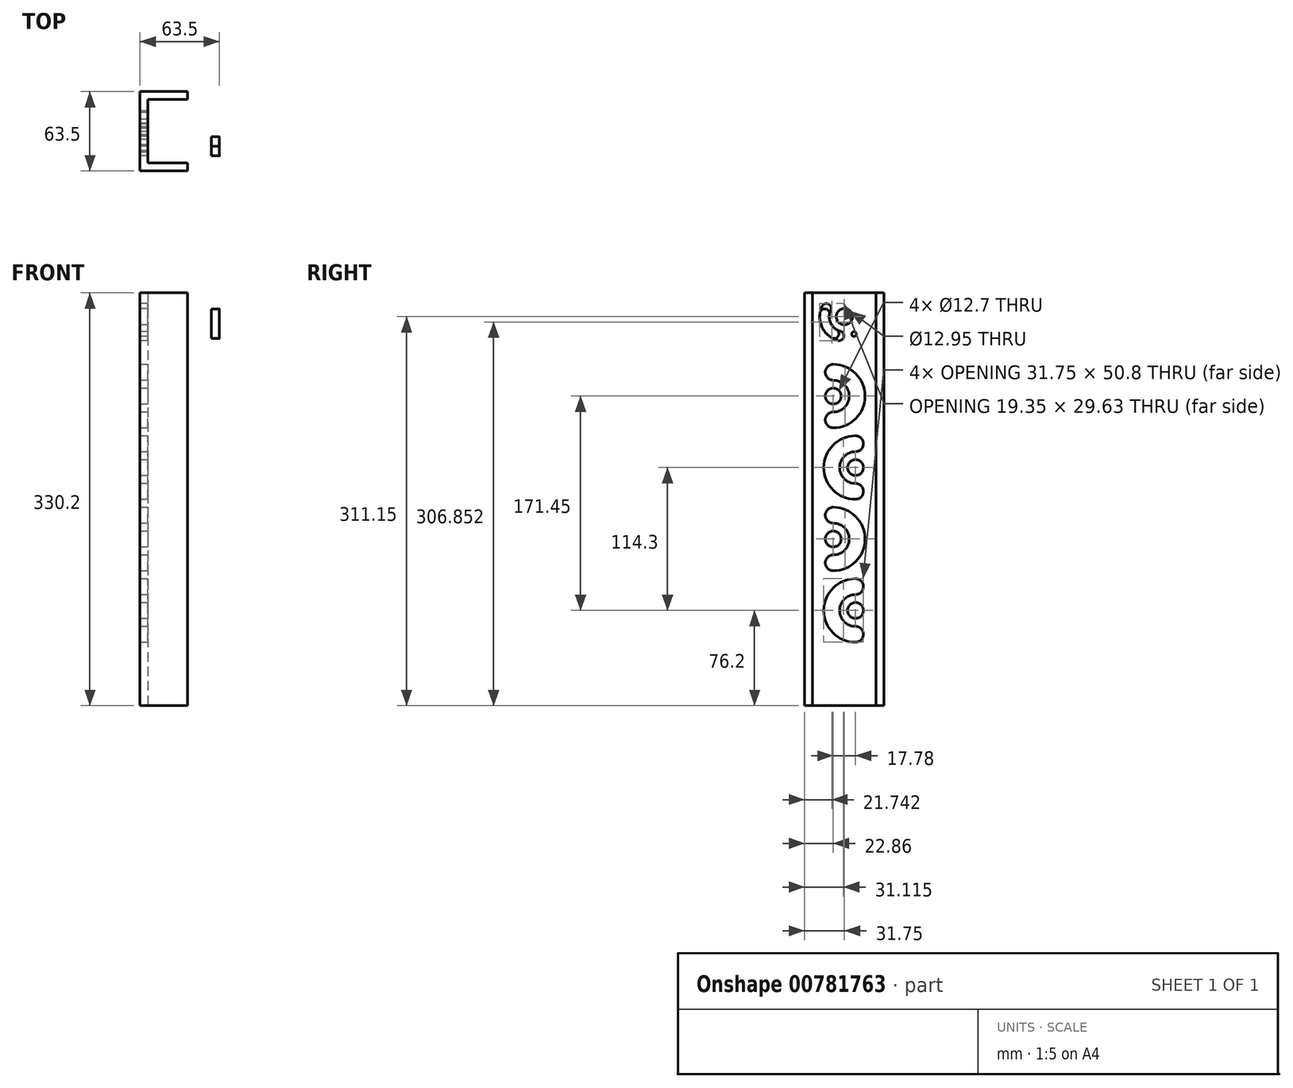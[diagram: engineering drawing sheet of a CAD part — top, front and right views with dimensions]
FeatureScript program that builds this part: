
annotation { "Feature Type Name" : "Feature", "Feature Type Description" : "" }
export const myFeature = defineFeature(function(context is Context, id is Id, definition is map)
    precondition{}
    {
        {
            var Q0;
            Q0=qCreatedBy(makeId("Top.planeOp"),FACE);
            var sketch = newSketch(context, id + "F0", { "sketchPlane" : qUnion([Q0])});
            skLineSegment(sketch, "E0.bottom", {"start": v(31.75, -31.75) * mm, "end": v(-31.75, -31.75) * mm});
            skLineSegment(sketch, "E0.top", {"start": v(31.75, 31.75) * mm, "end": v(-31.75, 31.75) * mm});
            skLineSegment(sketch, "E0.left", {"start": v(31.75, -31.75) * mm, "end": v(31.75, 31.75) * mm});
            skLineSegment(sketch, "E0.right", {"start": v(-31.75, -31.75) * mm, "end": v(-31.75, 31.75) * mm});
            skPoint(sketch, "E0.middle", {"position": v(0, 0) * mm});
            skLineSegment(sketch, "E1.bottom", {"start": v(25.4, -25.4) * mm, "end": v(-25.4, -25.4) * mm});
            skLineSegment(sketch, "E1.top", {"start": v(25.4, 25.4) * mm, "end": v(-25.4, 25.4) * mm});
            skLineSegment(sketch, "E1.left", {"start": v(25.4, -25.4) * mm, "end": v(25.4, 25.4) * mm});
            skLineSegment(sketch, "E1.right", {"start": v(-25.4, -25.4) * mm, "end": v(-25.4, 25.4) * mm});
            skSolve(sketch);
        }
        {
            var Q0;
            Q0=makeQuery(id+"F0.imprint","IMPRINT",FACE,{"disambiguationData":[TD([[makeQuery(id+"F0.imprint","IMPRINT",EDGE,{"derivedFrom":sQuery(id+"F0.wireOp",EDGE,"E0.bottom")}),-1.0]])]});
            extrude(context, id + "F1", {"entities" : qUnion([Q0]), "endBound" : BoundingType.SYMMETRIC, "depth" : 330.2 * mm, "offsetDistance" : 25.4 * mm});
        }
        {
            var Q0;
            Q0=makeQuery(id+"F1.opExtrude","SWEPT_FACE",FACE,{"disambiguationData":[OSD([sQuery(id+"F0.wireOp",EDGE,"E0.right")])]});
            var sketch = newSketch(context, id + "F2", { "sketchPlane" : qUnion([Q0])});
            skSolve(sketch);
        }
        {
            var Q0;
            Q0=makeQuery(id+"F1.opExtrude","SWEPT_FACE",FACE,{"disambiguationData":[OSD([sQuery(id+"F0.wireOp",EDGE,"E0.left")])]});
            var sketch = newSketch(context, id + "F3", { "sketchPlane" : qUnion([Q0])});
            skLineSegment(sketch, "E2.0", {"start": v(-31.75, 165.1) * mm, "end": v(31.75, 165.1) * mm, "construction": true});
            skLineSegment(sketch, "E2.1", {"start": v(-31.75, 165.1) * mm, "end": v(-31.75, -165.1) * mm, "construction": true});
            skLineSegment(sketch, "E2.2", {"start": v(31.75, 165.1) * mm, "end": v(31.75, -165.1) * mm, "construction": true});
            skLineSegment(sketch, "E2.3", {"start": v(-31.75, -165.1) * mm, "end": v(31.75, -165.1) * mm, "construction": true});
            skCircle(sketch, "E3", {"center": v(0, 146.05) * mm, "radius": 6.48 * mm});
            skArc(sketch, "E4", {"start": v(17.84, 137.73) * mm, "mid": v(19.5, 143.31) * mm, "end": v(19.44, 149.13) * mm});
            skArc(sketch, "E5", {"start": v(10.93, 140.95) * mm, "mid": v(11.95, 144.37) * mm, "end": v(11.92, 147.94) * mm});
            skLineSegment(sketch, "E6", {"start": v(0, 146.05) * mm, "end": v(19.44, 149.13) * mm, "construction": true});
            skLineSegment(sketch, "E7", {"start": v(0, 146.05) * mm, "end": v(9.54, 128.83) * mm, "construction": true});
            skLineSegment(sketch, "E8", {"start": v(0, 146.05) * mm, "end": v(24.19, 134.77) * mm, "construction": true});
            skCircle(sketch, "E9", {"center": v(0, 146.05) * mm, "radius": 15.88 * mm, "construction": true});
            skArc(sketch, "E10", {"start": v(11.92, 147.94) * mm, "mid": v(15.08, 152.3) * mm, "end": v(19.44, 149.13) * mm});
            skArc(sketch, "E11.MirrorCS", {"start": v(6.21, 135.7) * mm, "mid": v(4.91, 130.48) * mm, "end": v(10.14, 129.18) * mm});
            skArc(sketch, "E12.MirrorCS", {"start": v(10.93, 140.95) * mm, "mid": v(8.97, 137.98) * mm, "end": v(6.21, 135.7) * mm});
            skArc(sketch, "E13.MirrorCS", {"start": v(17.84, 137.73) * mm, "mid": v(14.63, 132.88) * mm, "end": v(10.14, 129.18) * mm});
            skLineSegment(sketch, "E14", {"start": v(0, 146.05) * mm, "end": v(-19.11, 146.05) * mm, "construction": true});
            skLineSegment(sketch, "E15", {"start": v(0, 146.05) * mm, "end": v(0, 119.4) * mm, "construction": true});
            skArc(sketch, "E16.MirrorCS", {"start": v(-6.21, 135.7) * mm, "mid": v(-4.91, 130.48) * mm, "end": v(-10.14, 129.18) * mm});
            skArc(sketch, "E17.MirrorCS", {"start": v(-17.84, 137.73) * mm, "mid": v(-14.63, 132.88) * mm, "end": v(-10.14, 129.18) * mm});
            skArc(sketch, "E18.MirrorCS", {"start": v(-17.84, 137.73) * mm, "mid": v(-19.5, 143.31) * mm, "end": v(-19.44, 149.13) * mm});
            skArc(sketch, "E19.MirrorCS", {"start": v(-11.92, 147.94) * mm, "mid": v(-15.08, 152.3) * mm, "end": v(-19.44, 149.13) * mm});
            skArc(sketch, "E20.MirrorCS", {"start": v(-10.93, 140.95) * mm, "mid": v(-11.95, 144.37) * mm, "end": v(-11.92, 147.94) * mm});
            skArc(sketch, "E21.MirrorCS", {"start": v(-10.93, 140.95) * mm, "mid": v(-8.97, 137.98) * mm, "end": v(-6.21, 135.7) * mm});
            skSolve(sketch);
        }
        {
            var Q0;
            Q0=makeQuery(id+"F3.imprint","IMPRINT",FACE,{"disambiguationData":[TD([[makeQuery(id+"F3.imprint","IMPRINT",EDGE,{"derivedFrom":sQuery(id+"F3.wireOp",EDGE,"E3")}),1.0]])]});
            var Q1;
            Q1=makeQuery(id+"F3.imprint","IMPRINT",FACE,{"disambiguationData":[TD([[makeQuery(id+"F3.imprint","IMPRINT",EDGE,{"derivedFrom":sQuery(id+"F3.wireOp",EDGE,"E4")}),1.0]])]});
            var Q2;
            Q2=makeQuery(id+"F3.imprint","IMPRINT",FACE,{"disambiguationData":[TD([[makeQuery(id+"F3.imprint","IMPRINT",EDGE,{"derivedFrom":sQuery(id+"F3.wireOp",EDGE,"E16.MirrorCS")}),-1.0]])]});
            extrude(context, id + "F4", {"entities" : qUnion([Q0, Q1, Q2]), "operationType" : NewBodyOperationType.REMOVE, "oppositeDirection" : true, "depth" : 25.4 * mm, "offsetDistance" : 25.4 * mm});
        }
        {
            var Q0;
            {var subQ0=sQuery(id+"F0.wireOp",EDGE,"E0.right");Q0=makeQuery(id+"F2.imprint","IMPRINT",FACE,{"disambiguationData":[TD([[makeQuery(id+"F2.imprint","IMPRINT",EDGE,{"derivedFrom":makeQuery(id+"F1.opExtrude","CAP_EDGE",EDGE,{"disambiguationData":[OSD([subQ0])],"isStart":true})}),-1.0]])]});}
            var sketch = newSketch(context, id + "F5", { "sketchPlane" : qUnion([Q0])});
            skCircle(sketch, "E22.0", {"center": v(0, 146.05) * mm, "radius": 6.48 * mm});
            skCircle(sketch, "E23", {"center": v(-7.7, 132.17) * mm, "radius": 1.9 * mm});
            skArc(sketch, "E24", {"start": v(5.1, 127.04) * mm, "mid": v(17.84, 137.73) * mm, "end": v(17.84, 154.37) * mm});
            skCircle(sketch, "E25", {"center": v(0, 146.05) * mm, "radius": 15.88 * mm, "construction": true});
            skLineSegment(sketch, "E26", {"start": v(0, 146.05) * mm, "end": v(5.1, 127.04) * mm, "construction": true});
            skLineSegment(sketch, "E27", {"start": v(0, 146.05) * mm, "end": v(-15.88, 146.05) * mm, "construction": true});
            skLineSegment(sketch, "E28", {"start": v(0, 146.05) * mm, "end": v(17.84, 154.37) * mm, "construction": true});
            skArc(sketch, "E29", {"start": v(3.12, 134.4) * mm, "mid": v(10.93, 140.95) * mm, "end": v(10.93, 151.15) * mm});
            skLineSegment(sketch, "E30", {"start": v(0, 146.05) * mm, "end": v(-7.7, 132.17) * mm});
            skArc(sketch, "E31", {"start": v(3.12, 134.4) * mm, "mid": v(0.43, 129.73) * mm, "end": v(5.1, 127.04) * mm});
            skArc(sketch, "E32", {"start": v(17.84, 154.37) * mm, "mid": v(12.78, 156.21) * mm, "end": v(10.93, 151.15) * mm});
            skCircle(sketch, "E33", {"center": v(-7.7, 132.17) * mm, "radius": 3.18 * mm, "construction": true});
            skLineSegment(sketch, "E34", {"start": v(0, 146.05) * mm, "end": v(-15.58, 149.08) * mm, "construction": true});
            skCircle(sketch, "E35", {"center": v(-15.58, 149.08) * mm, "radius": 3.18 * mm, "construction": true});
            skArc(sketch, "E36.0", {"start": v(-11.92, 147.94) * mm, "mid": v(-15.08, 152.3) * mm, "end": v(-19.44, 149.13) * mm, "construction": true});
            skLineSegment(sketch, "E37", {"start": v(0, 146.05) * mm, "end": v(-15.68, 148.53) * mm, "construction": true});
            skSolve(sketch);
        }
        {
            var Q0;
            Q0 = qSketchRegion(id + "F5", true);
            extrude(context, id + "F6", {"entities" : qUnion([Q0]), "operationType" : NewBodyOperationType.REMOVE, "oppositeDirection" : true, "depth" : 25.4 * mm, "offsetDistance" : 25.4 * mm});
        }
        {
            var Q0;
            Q0=makeQuery(id+"F1.opExtrude","SWEPT_FACE",FACE,{"disambiguationData":[OSD([sQuery(id+"F0.wireOp",EDGE,"E0.left")])]});
            var sketch = newSketch(context, id + "F7", { "sketchPlane" : qUnion([Q0])});
            skArc(sketch, "E38", {"start": v(-8.89, 101.6) * mm, "mid": v(10.16, 82.55) * mm, "end": v(-8.89, 63.5) * mm, "construction": true});
            skArc(sketch, "E39.0", {"start": v(-8.89, 95.25) * mm, "mid": v(3.81, 82.55) * mm, "end": v(-8.89, 69.85) * mm});
            skArc(sketch, "E40.0", {"start": v(-8.89, 107.95) * mm, "mid": v(16.5, 82.55) * mm, "end": v(-8.89, 57.15) * mm});
            skArc(sketch, "E41", {"start": v(-8.89, 107.95) * mm, "mid": v(-15.24, 101.6) * mm, "end": v(-8.89, 95.25) * mm});
            skArc(sketch, "E42", {"start": v(-8.89, 57.15) * mm, "mid": v(-15.24, 63.5) * mm, "end": v(-8.89, 69.85) * mm});
            skArc(sketch, "E43", {"start": v(8.9, 6.35) * mm, "mid": v(-10.16, 25.4) * mm, "end": v(8.9, 44.45) * mm, "construction": true});
            skArc(sketch, "E44.0", {"start": v(8.9, 12.7) * mm, "mid": v(-3.8, 25.4) * mm, "end": v(8.9, 38.1) * mm});
            skArc(sketch, "E45.0", {"start": v(8.9, 0) * mm, "mid": v(-16.5, 25.4) * mm, "end": v(8.89, 50.8) * mm});
            skArc(sketch, "E46", {"start": v(8.9, 0) * mm, "mid": v(15.24, 6.35) * mm, "end": v(8.9, 12.7) * mm});
            skArc(sketch, "E47", {"start": v(8.9, 50.8) * mm, "mid": v(15.24, 44.45) * mm, "end": v(8.9, 38.1) * mm});
            skArc(sketch, "E48", {"start": v(-8.89, -12.7) * mm, "mid": v(10.16, -31.75) * mm, "end": v(-8.89, -50.8) * mm, "construction": true});
            skArc(sketch, "E49.0", {"start": v(-8.89, -19.05) * mm, "mid": v(3.81, -31.75) * mm, "end": v(-8.89, -44.45) * mm});
            skArc(sketch, "E50.0", {"start": v(-8.89, -6.35) * mm, "mid": v(16.5, -31.75) * mm, "end": v(-8.89, -57.15) * mm});
            skArc(sketch, "E51", {"start": v(-8.89, -6.35) * mm, "mid": v(-15.24, -12.7) * mm, "end": v(-8.89, -19.05) * mm});
            skArc(sketch, "E52", {"start": v(-8.89, -57.15) * mm, "mid": v(-15.24, -50.8) * mm, "end": v(-8.89, -44.45) * mm});
            skArc(sketch, "E53", {"start": v(8.9, -107.95) * mm, "mid": v(-10.16, -88.9) * mm, "end": v(8.89, -69.85) * mm, "construction": true});
            skArc(sketch, "E54.0", {"start": v(8.9, -101.6) * mm, "mid": v(-3.8, -88.9) * mm, "end": v(8.89, -76.2) * mm});
            skArc(sketch, "E55.0", {"start": v(8.9, -114.3) * mm, "mid": v(-16.5, -88.9) * mm, "end": v(8.89, -63.5) * mm});
            skArc(sketch, "E56", {"start": v(8.9, -114.3) * mm, "mid": v(15.24, -107.95) * mm, "end": v(8.9, -101.6) * mm});
            skArc(sketch, "E57", {"start": v(8.89, -63.5) * mm, "mid": v(15.24, -69.85) * mm, "end": v(8.89, -76.2) * mm});
            skCircle(sketch, "E58", {"center": v(-8.89, 82.55) * mm, "radius": 6.35 * mm});
            skCircle(sketch, "E59", {"center": v(8.9, 25.4) * mm, "radius": 6.35 * mm});
            skCircle(sketch, "E60", {"center": v(8.9, -88.9) * mm, "radius": 6.35 * mm});
            skCircle(sketch, "E61", {"center": v(-8.89, -31.75) * mm, "radius": 6.35 * mm});
            skSolve(sketch);
        }
        {
            var Q0;
            Q0 = qSketchRegion(id + "F7", true);
            extrude(context, id + "F8", {"entities" : qUnion([Q0]), "operationType" : NewBodyOperationType.REMOVE, "endBound" : BoundingType.THROUGH_ALL, "oppositeDirection" : true, "depth" : 25.4 * mm, "offsetDistance" : 25.4 * mm});
        }
    });
